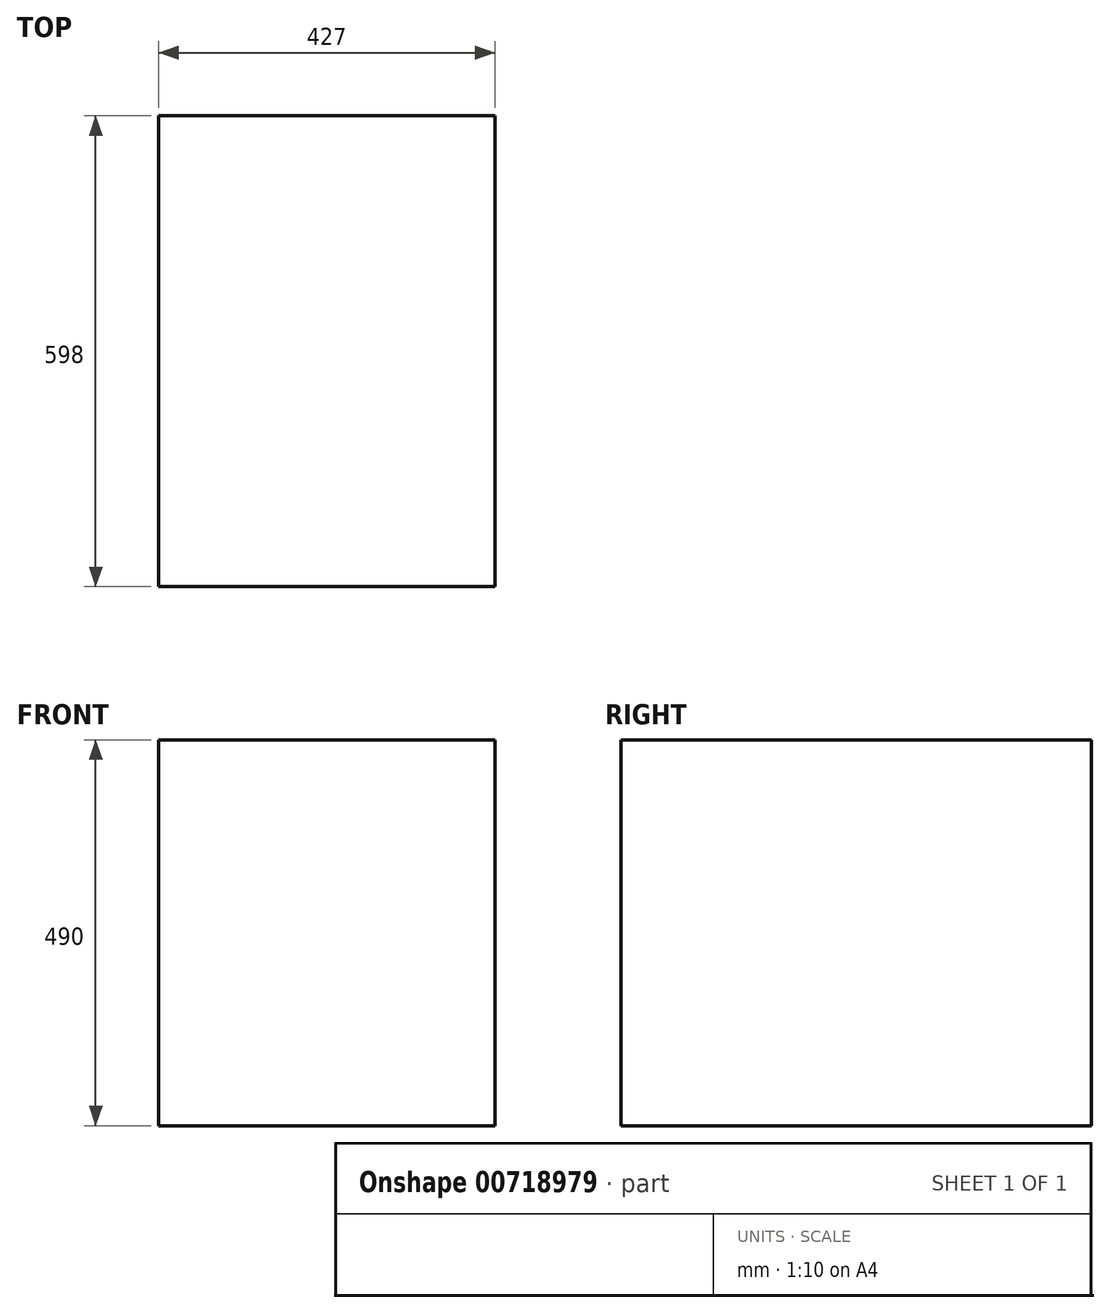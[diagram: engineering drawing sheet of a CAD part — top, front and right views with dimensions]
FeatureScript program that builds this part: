
annotation { "Feature Type Name" : "Feature", "Feature Type Description" : "" }
export const myFeature = defineFeature(function(context is Context, id is Id, definition is map)
    precondition{}
    {
        {
            var Q0;
            Q0=qCreatedBy(makeId("Top.planeOp"),FACE);
            var sketch = newSketch(context, id + "F0", { "sketchPlane" : qUnion([Q0])});
            skLineSegment(sketch, "E0.bottom", {"start": v(-213.5, 299) * mm, "end": v(213.5, 299) * mm});
            skLineSegment(sketch, "E0.top", {"start": v(-213.5, -299) * mm, "end": v(213.5, -299) * mm});
            skLineSegment(sketch, "E0.left", {"start": v(-213.5, 299) * mm, "end": v(-213.5, -299) * mm});
            skLineSegment(sketch, "E0.right", {"start": v(213.5, 299) * mm, "end": v(213.5, -299) * mm});
            skSolve(sketch);
        }
        {
            var Q0;
            Q0=makeQuery(id+"F0.imprint","IMPRINT",FACE,{"disambiguationData":[TD([[makeQuery(id+"F0.imprint","IMPRINT",EDGE,{"derivedFrom":sQuery(id+"F0.wireOp",EDGE,"E0.bottom")}),-1.0]])]});
            extrude(context, id + "F1", {"entities" : qUnion([Q0]), "depth" : 490 * mm, "offsetDistance" : 25 * mm});
        }
    });
